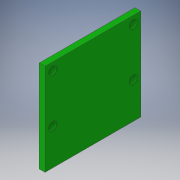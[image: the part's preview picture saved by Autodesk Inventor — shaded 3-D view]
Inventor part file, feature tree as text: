
AUTODESK INVENTOR PART (.ipt)
format: ipt  version: 2018 (Build 220112000, 112)  size: 103,424 bytes
history: native  units: in
note: dims shown in document units (in); Inventor stores cm internally (conversion verified against a paired STEP export)
features: extrude x1, sketch x1
ambient origin geometry x8: Origin, YZ Plane, XZ Plane, XY Plane, X Axis, Y Axis, Z Axis, Center Point
bodies: Solid1 (feature_tree)
feature tree (2):
  extrude  "Extrusion1"  Depth=0.9843in
  sketch  "Sketch1"  dims[d0=0.9449in d1=0.9843in d2=0.0827in d3=0.0787in d4=0.0787in d5=0.0827in d6=0.4921in d7=0.0787in d8=0.0591in d9=0.0in]
